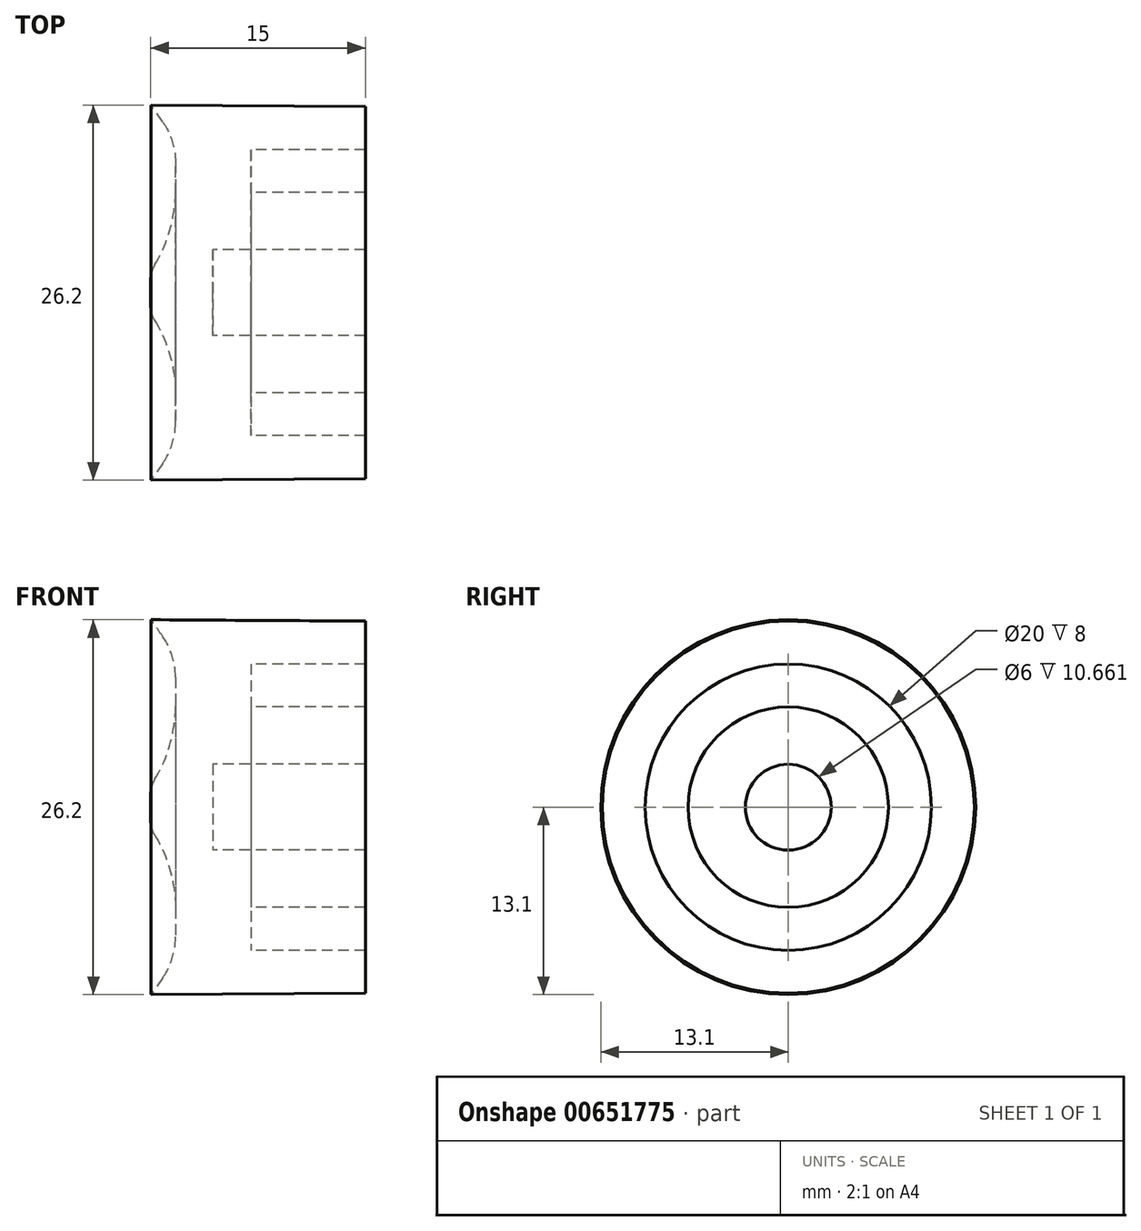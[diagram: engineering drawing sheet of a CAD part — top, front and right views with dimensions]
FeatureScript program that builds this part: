
annotation { "Feature Type Name" : "Feature", "Feature Type Description" : "" }
export const myFeature = defineFeature(function(context is Context, id is Id, definition is map)
    precondition{}
    {
        {
            var Q0;
            Q0=qCreatedBy(makeId("Front.planeOp"),FACE);
            var sketch = newSketch(context, id + "F0", { "sketchPlane" : qUnion([Q0])});
            skLineSegment(sketch, "E0", {"start": v(0, 0) * mm, "end": v(0, 3) * mm, "construction": true});
            skLineSegment(sketch, "E1", {"start": v(15, 3) * mm, "end": v(15, 7) * mm});
            skLineSegment(sketch, "E2", {"start": v(15, 7) * mm, "end": v(7, 7) * mm});
            skLineSegment(sketch, "E3", {"start": v(7, 7) * mm, "end": v(7, 10) * mm});
            skLineSegment(sketch, "E4", {"start": v(15, 10) * mm, "end": v(7, 10) * mm});
            skLineSegment(sketch, "E5", {"start": v(15, 10) * mm, "end": v(15, 13) * mm});
            skLineSegment(sketch, "E6", {"start": v(0.03, 13.1) * mm, "end": v(15, 13) * mm});
            skLineSegment(sketch, "E7", {"start": v(0.03, 13.1) * mm, "end": v(0.85, 11.9) * mm});
            skLineSegment(sketch, "E8", {"start": v(1.73, 9.07) * mm, "end": v(1.73, 7.13) * mm});
            skPoint(sketch, "E9.visualSharp", {"position": v(1.73, 10.63) * mm});
            skArc(sketch, "E9.filletArc", {"start": v(1.73, 9.07) * mm, "mid": v(1.5, 10.56) * mm, "end": v(0.85, 11.9) * mm});
            skLineSegment(sketch, "E10", {"start": v(0.52, 0) * mm, "end": v(15.52, 0) * mm, "construction": true});
            skLineSegment(sketch, "E11", {"start": v(15, 3) * mm, "end": v(4.34, 3) * mm});
            skLineSegment(sketch, "E12", {"start": v(4.34, 3) * mm, "end": v(4.34, 0) * mm});
            skLineSegment(sketch, "E13", {"start": v(0, 0) * mm, "end": v(4.34, 0) * mm});
            skLineSegment(sketch, "E14", {"start": v(0, 0) * mm, "end": v(0, 0.91) * mm});
            skArc(sketch, "E15", {"start": v(0.29, 1.95) * mm, "mid": v(1.37, 4.44) * mm, "end": v(1.73, 7.13) * mm});
            skPoint(sketch, "E16.visualSharp", {"position": v(0, 1.5) * mm});
            skArc(sketch, "E16.filletArc", {"start": v(0.29, 1.95) * mm, "mid": v(0.07, 1.45) * mm, "end": v(0, 0.91) * mm});
            skSolve(sketch);
        }
        {
            var Q0;
            Q0=makeQuery(id+"F0.imprint","IMPRINT",FACE,{"disambiguationData":[TD([[makeQuery(id+"F0.imprint","IMPRINT",EDGE,{"derivedFrom":sQuery(id+"F0.wireOp",EDGE,"E1")}),1.0]])]});
            var Q1;
            Q1=sQuery(id+"F0.wireOp",EDGE,"E10");
            revolve(context, id + "F1", {"surfaceOperationType" : NewSurfaceOperationType.NEW, "entities" : qUnion([Q0]), "axis" : qUnion([Q1]), "revolveType" : RevolveType.FULL});
        }
    });
